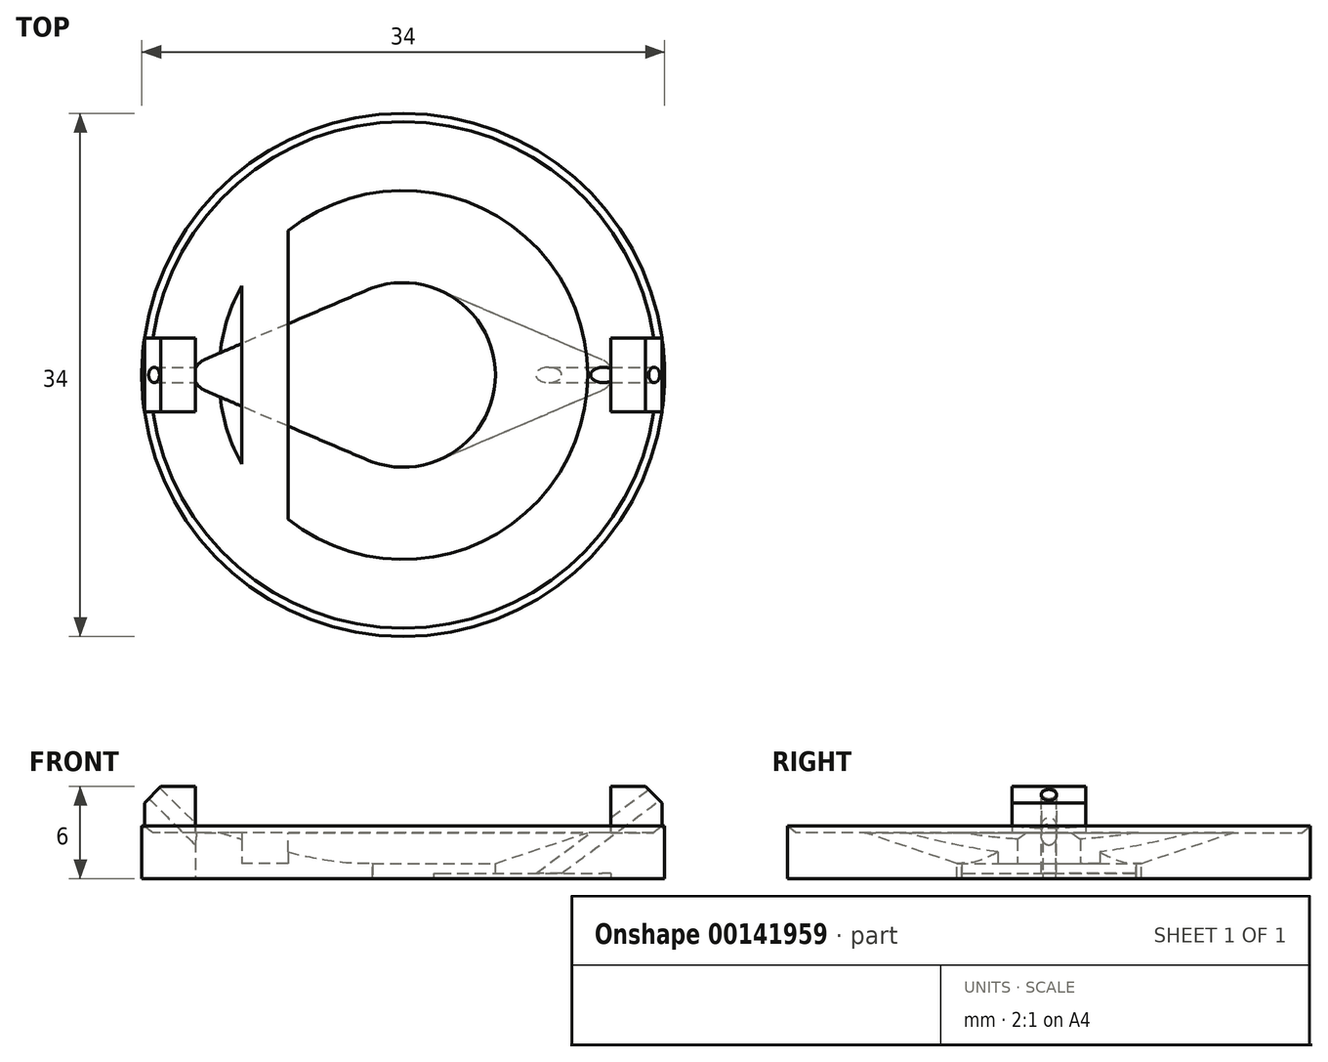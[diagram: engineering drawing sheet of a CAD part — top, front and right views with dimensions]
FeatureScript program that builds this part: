
annotation { "Feature Type Name" : "Feature", "Feature Type Description" : "" }
export const myFeature = defineFeature(function(context is Context, id is Id, definition is map)
    precondition{}
    {
        {
            var Q0;
            Q0=qCreatedBy(makeId("Front.planeOp"),FACE);
            var sketch = newSketch(context, id + "F0", { "sketchPlane" : qUnion([Q0])});
            skLineSegment(sketch, "E0", {"start": v(-12, 3) * mm, "end": v(-17, 3) * mm});
            skLineSegment(sketch, "E1", {"start": v(-17, 3) * mm, "end": v(-17, 0) * mm});
            skLineSegment(sketch, "E2", {"start": v(-17, 0) * mm, "end": v(-6, 0) * mm});
            skLineSegment(sketch, "E3", {"start": v(-6, 0) * mm, "end": v(-6, 1) * mm});
            skLineSegment(sketch, "E4", {"start": v(-6, 1) * mm, "end": v(-12, 3) * mm});
            skLineSegment(sketch, "E5", {"start": v(0, 14.08) * mm, "end": v(0, -13.4) * mm});
            skLineSegment(sketch, "E6", {"start": v(-17, 3) * mm, "end": v(-17, 3.43) * mm});
            skLineSegment(sketch, "E7", {"start": v(-17, 3.43) * mm, "end": v(-16.46, 3) * mm});
            skSolve(sketch);
        }
        {
            var Q0;
            Q0=makeQuery(id+"F0.imprint","IMPRINT",FACE,{"disambiguationData":[TD([[makeQuery(id+"F0.imprint","IMPRINT",EDGE,{"derivedFrom":sQuery(id+"F0.wireOp",EDGE,"E0")}),1.0]])]});
            var Q1;
            {var subQ0=sQuery(id+"F0.wireOp",EDGE,"E6");Q1=makeQuery(id+"F0.imprint","IMPRINT",FACE,{"disambiguationData":[TD([[makeQuery(id+"F0.imprint","IMPRINT",EDGE,{"derivedFrom":subQ0}),-1.0]])]});}
            var Q2;
            Q2=sQuery(id+"F0.wireOp",EDGE,"E5");
            revolve(context, id + "F1", {"entities" : qUnion([Q0, Q1]), "axis" : qUnion([Q2]), "revolveType" : RevolveType.FULL});
        }
        {
            var Q0;
            Q0=qCreatedBy(makeId("Top.planeOp"),FACE);
            var sketch = newSketch(context, id + "F2", { "sketchPlane" : qUnion([Q0])});
            skLineSegment(sketch, "E8", {"start": v(2, 5.67) * mm, "end": v(12.93, 1) * mm});
            skLineSegment(sketch, "E9.MirrorCS", {"start": v(2, -5.67) * mm, "end": v(12.93, -1) * mm});
            skArc(sketch, "E10", {"start": v(12.93, -1) * mm, "mid": v(13.59, 0) * mm, "end": v(12.93, 1) * mm});
            skLineSegment(sketch, "E11.MirrorCS", {"start": v(-2, 5.67) * mm, "end": v(-12.93, 1) * mm});
            skArc(sketch, "E12.MirrorCS", {"start": v(-12.93, -1) * mm, "mid": v(-13.59, 0) * mm, "end": v(-12.93, 1) * mm});
            skLineSegment(sketch, "E13.MirrorCS", {"start": v(-2, -5.67) * mm, "end": v(-12.93, -1) * mm});
            skLineSegment(sketch, "E14", {"start": v(2, -5.67) * mm, "end": v(2, 5.67) * mm});
            skLineSegment(sketch, "E15", {"start": v(-2, -5.67) * mm, "end": v(-2, 5.67) * mm});
            skSolve(sketch);
        }
        {
            var Q0;
            Q0=makeQuery(id+"F2.imprint","IMPRINT",FACE,{"disambiguationData":[TD([[makeQuery(id+"F2.imprint","IMPRINT",EDGE,{"derivedFrom":sQuery(id+"F2.wireOp",EDGE,"E8")}),-1.0]])]});
            extrude(context, id + "F3", {"entities" : qUnion([Q0]), "operationType" : NewBodyOperationType.REMOVE, "depth" : 0.35 * mm});
        }
        {
            var Q0;
            Q0=makeQuery(id+"F2.imprint","IMPRINT",FACE,{"disambiguationData":[TD([[makeQuery(id+"F2.imprint","IMPRINT",EDGE,{"derivedFrom":sQuery(id+"F2.wireOp",EDGE,"E11.MirrorCS")}),1.0]])]});
            extrude(context, id + "F4", {"entities" : qUnion([Q0]), "operationType" : NewBodyOperationType.REMOVE, "depth" : 5 * mm});
        }
        {
            var Q0;
            Q0=qCreatedBy(makeId("Top.planeOp"),FACE);
            var sketch = newSketch(context, id + "F5", { "sketchPlane" : qUnion([Q0])});
            skLineSegment(sketch, "E16.bottom", {"start": v(-16.83, -2.39) * mm, "end": v(-13.5, -2.39) * mm});
            skLineSegment(sketch, "E16.top", {"start": v(-16.83, 2.39) * mm, "end": v(-13.5, 2.39) * mm});
            skLineSegment(sketch, "E16.left", {"start": v(-16.83, -2.39) * mm, "end": v(-16.83, 2.39) * mm});
            skLineSegment(sketch, "E16.right", {"start": v(-13.5, -2.39) * mm, "end": v(-13.5, 2.39) * mm});
            skLineSegment(sketch, "E17.MirrorCS", {"start": v(16.83, -2.39) * mm, "end": v(16.83, 2.39) * mm});
            skLineSegment(sketch, "E18.MirrorCS", {"start": v(16.83, 2.39) * mm, "end": v(13.5, 2.39) * mm});
            skLineSegment(sketch, "E19.MirrorCS", {"start": v(13.5, -2.39) * mm, "end": v(13.5, 2.39) * mm});
            skLineSegment(sketch, "E20.MirrorCS", {"start": v(16.83, -2.39) * mm, "end": v(13.5, -2.39) * mm});
            skSolve(sketch);
        }
        {
            var Q0;
            Q0=makeQuery(id+"F5.imprint","IMPRINT",FACE,{"disambiguationData":[TD([[makeQuery(id+"F5.imprint","IMPRINT",EDGE,{"derivedFrom":sQuery(id+"F5.wireOp",EDGE,"E16.bottom")}),1.0]])]});
            var Q1;
            Q1=makeQuery(id+"F5.imprint","IMPRINT",FACE,{"disambiguationData":[TD([[makeQuery(id+"F5.imprint","IMPRINT",EDGE,{"derivedFrom":sQuery(id+"F5.wireOp",EDGE,"E17.MirrorCS")}),1.0]])]});
            extrude(context, id + "F6", {"entities" : qUnion([Q0, Q1]), "operationType" : NewBodyOperationType.ADD, "depth" : 6 * mm});
        }
        {
            var Q0;
            Q0=qCreatedBy(makeId("Top.planeOp"),FACE);
            var sketch = newSketch(context, id + "F7", { "sketchPlane" : qUnion([Q0])});
            skLineSegment(sketch, "E21.bottom", {"start": v(-10.5, -10.38) * mm, "end": v(-7.5, -10.38) * mm});
            skLineSegment(sketch, "E21.top", {"start": v(-10.5, 10.38) * mm, "end": v(-7.5, 10.38) * mm});
            skLineSegment(sketch, "E21.left", {"start": v(-10.5, -10.38) * mm, "end": v(-10.5, 10.38) * mm});
            skLineSegment(sketch, "E21.right", {"start": v(-7.5, -10.38) * mm, "end": v(-7.5, 10.38) * mm});
            skSolve(sketch);
        }
        {
            var Q0;
            Q0=makeQuery(id+"F7.imprint","IMPRINT",FACE,{"disambiguationData":[TD([[makeQuery(id+"F7.imprint","IMPRINT",EDGE,{"derivedFrom":sQuery(id+"F7.wireOp",EDGE,"E21.bottom")}),1.0]])]});
            extrude(context, id + "F8", {"entities" : qUnion([Q0]), "operationType" : NewBodyOperationType.ADD, "depth" : 3 * mm, "hasSecondDirection" : true, "secondDirectionOppositeDirection" : false, "secondDirectionDepth" : 1 * mm});
        }
        {
            var Q0;
            Q0=qCreatedBy(makeId("Front.planeOp"),FACE);
            var sketch = newSketch(context, id + "F9", { "sketchPlane" : qUnion([Q0])});
            skLineSegment(sketch, "E22", {"start": v(9, 0) * mm, "end": v(17.01, 5.96) * mm});
            skLineSegment(sketch, "E23", {"start": v(8.3, 0.1) * mm, "end": v(16.7, 6.35) * mm});
            skLineSegment(sketch, "E24", {"start": v(8.3, 0.1) * mm, "end": v(9, 0) * mm});
            skLineSegment(sketch, "E25", {"start": v(17.01, 5.96) * mm, "end": v(16.7, 6.35) * mm});
            skLineSegment(sketch, "E26", {"start": v(-17.13, 5.79) * mm, "end": v(-12.5, 1.17) * mm});
            skLineSegment(sketch, "E27", {"start": v(-12.5, 1.17) * mm, "end": v(-12.16, 1.52) * mm});
            skLineSegment(sketch, "E28", {"start": v(-12.16, 1.52) * mm, "end": v(-16.77, 6.14) * mm});
            skLineSegment(sketch, "E29", {"start": v(-16.77, 6.14) * mm, "end": v(-17.13, 5.79) * mm});
            skLineSegment(sketch, "E30", {"start": v(-17.26, 4.5) * mm, "end": v(-15.14, 6.62) * mm});
            skLineSegment(sketch, "E31", {"start": v(-15.14, 6.62) * mm, "end": v(-17.08, 8.55) * mm});
            skLineSegment(sketch, "E32", {"start": v(-17.08, 8.55) * mm, "end": v(-19.23, 6.4) * mm});
            skLineSegment(sketch, "E33", {"start": v(-19.23, 6.4) * mm, "end": v(-17.26, 4.5) * mm});
            skLineSegment(sketch, "E34", {"start": v(0, 11.56) * mm, "end": v(0, -6.2) * mm});
            skLineSegment(sketch, "E35.MirrorCS", {"start": v(19.23, 6.4) * mm, "end": v(17.26, 4.5) * mm});
            skLineSegment(sketch, "E36.MirrorCS", {"start": v(17.26, 4.5) * mm, "end": v(15.14, 6.62) * mm});
            skLineSegment(sketch, "E37.MirrorCS", {"start": v(17.08, 8.55) * mm, "end": v(19.23, 6.4) * mm});
            skLineSegment(sketch, "E38.MirrorCS", {"start": v(15.14, 6.62) * mm, "end": v(17.08, 8.55) * mm});
            skSolve(sketch);
        }
        {
            var Q0;
            Q0=makeQuery(id+"F9.imprint","IMPRINT",FACE,{"disambiguationData":[TD([[makeQuery(id+"F9.imprint","IMPRINT",EDGE,{"derivedFrom":sQuery(id+"F9.wireOp",EDGE,"E22")}),1.0]])]});
            var Q1;
            Q1=sQuery(id+"F9.wireOp",EDGE,"E22");
            revolve(context, id + "F10", {"operationType" : NewBodyOperationType.REMOVE, "entities" : qUnion([Q0]), "axis" : qUnion([Q1]), "revolveType" : RevolveType.FULL, "oppositeDirection" : true});
        }
        {
            var Q0;
            Q0=makeQuery(id+"F9.imprint","IMPRINT",FACE,{"disambiguationData":[TD([[makeQuery(id+"F9.imprint","IMPRINT",EDGE,{"derivedFrom":sQuery(id+"F9.wireOp",EDGE,"E26")}),1.0]])]});
            var Q1;
            Q1=sQuery(id+"F9.wireOp",EDGE,"E28");
            revolve(context, id + "F11", {"operationType" : NewBodyOperationType.REMOVE, "entities" : qUnion([Q0]), "axis" : qUnion([Q1]), "revolveType" : RevolveType.FULL});
        }
        {
            var Q0;
            {var subQ4=sQuery(id+"F9.wireOp",EDGE,"E29");Q0=makeQuery(id+"F9.imprint","IMPRINT",FACE,{"disambiguationData":[TD([[makeQuery(id+"F9.imprint","IMPRINT",EDGE,{"derivedFrom":subQ4}),-1.0]])]});}
            var Q1;
            {var subQ0=sQuery(id+"F9.wireOp",EDGE,"E29");Q1=makeQuery(id+"F9.imprint","IMPRINT",FACE,{"disambiguationData":[TD([[makeQuery(id+"F9.imprint","IMPRINT",EDGE,{"derivedFrom":subQ0}),1.0]])]});}
            var Q2;
            {var subQ0=sQuery(id+"F9.wireOp",EDGE,"E25");Q2=makeQuery(id+"F9.imprint","IMPRINT",FACE,{"disambiguationData":[TD([[makeQuery(id+"F9.imprint","IMPRINT",EDGE,{"derivedFrom":subQ0}),1.0]])]});}
            var Q3;
            {var subQ0=sQuery(id+"F9.wireOp",EDGE,"E25");Q3=makeQuery(id+"F9.imprint","IMPRINT",FACE,{"disambiguationData":[TD([[makeQuery(id+"F9.imprint","IMPRINT",EDGE,{"derivedFrom":subQ0}),-1.0]])]});}
            extrude(context, id + "F12", {"entities" : qUnion([Q0, Q1, Q2, Q3]), "operationType" : NewBodyOperationType.REMOVE, "endBound" : BoundingType.SYMMETRIC, "oppositeDirection" : true, "depth" : 5.8 * mm, "hasSecondDirection" : true, "secondDirectionOppositeDirection" : false, "secondDirectionDepth" : 25 * mm});
        }
    });
